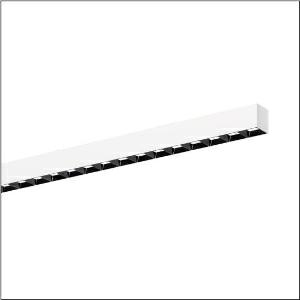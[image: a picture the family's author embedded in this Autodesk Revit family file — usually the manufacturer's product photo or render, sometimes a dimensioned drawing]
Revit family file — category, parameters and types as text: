
# Revit family: silica_r__21_51mx24tctaw_1b94
name_source: partatom
category: Lighting Fixtures
units: mm (PartAtom-declared; Revit-internal decimal feet)

## family parameters
Cut with Voids When Loaded = No
Host = Face
Light Source = No
Part Type = Normal
Room Calculation Point = No
Round Connector Dimension = Use Diameter
Shared = No

## types (1)
- --- (1 x LED, 8200 lm, 81.1 W, 6500K)
    Apparent Load = 81 VA
    CIE Flux Codes = 74 94 99 100 100
    Color Rendering = 80
    Color Temperature = 6500K
    Default Elevation = 1800 mm
    Description = Silica® 21, office luminaire, primary light control with darklight reflector, of PMMA, black, light emission: direct distribution, primary light characteristic: asymmetric, installation type: surface-mounted, LED, rated luminous flux: 8.200lm, luminous efficacy: 96lm/W, light colour: 8tw, colour temperature: 2700..6500K, control gear: ECG DALI, with terminal, 3+2-pole, max. 2.5mm², mains connection: 220..240V, AC, 50/60Hz, rated input power: 85.2W, luminaire housing, of aluminium, traffic white (RAL 9016), length: 3.004mm, width: 53mm, height: 53mm, protection rating (complete): IP20, insulation class (complete): insulation class I (protective earthing), certification: CE, permissible operating ambient temperature: 0..+35°C, standard: EN 50419, packaging unit: 1 piece
    Height = 0 mm  [stored 0 ft]
    Lamp = 1 x LED
    Lamp Light Flux = 8200 lm
    Lamp Power = 81.1 W
    Lamp count = 1
    Length = 3004 mm
    Luminous efficacy = 101 lm/W
    Manufacturer = Siteco
    ModVariant = No
    Model = 51MX24TCTAW
    Mounting Place = Ceiling
    Mounting Type = Recessed
    Number of Poles = 1
    OnlyDefault = Yes
    Power Factor = 1
    Product Name = Silica® 21
    Product group = office luminaire | ceiling recessed
    ProductGroupID = 400
    Protection Class = Protection class I
    Protection Degree = IP 20
    RLX_Detail_Level = 1
    RLX_Emergency_Light_Flux = 0 lm
    RLX_Emergency_Type = 0
    RLX_Emergency_Type_DB = No
    RlxData = <blob elided: 58949 chars, md5=b24c3414>
    Socket = socket
    Standby Power = 0 W
    System Light Flux = 8200 lm
    System Power = 81 W
    Type Comments = individual setting
    Type Image = l_1335873.jpg
    URL = http://relux.com
    VarID = @adj_109807
    Voltage = 0 V
    Weight = 0.00 kg
    Width = 53 mm

note: [stored X ft] marks values corroborated as IEEE doubles in the binary element streams (Revit-internal decimal feet)

## geometry (parser evidence)
native form markers: Blend x4, Sweep x11
no freeform markers — native parametric forms only
